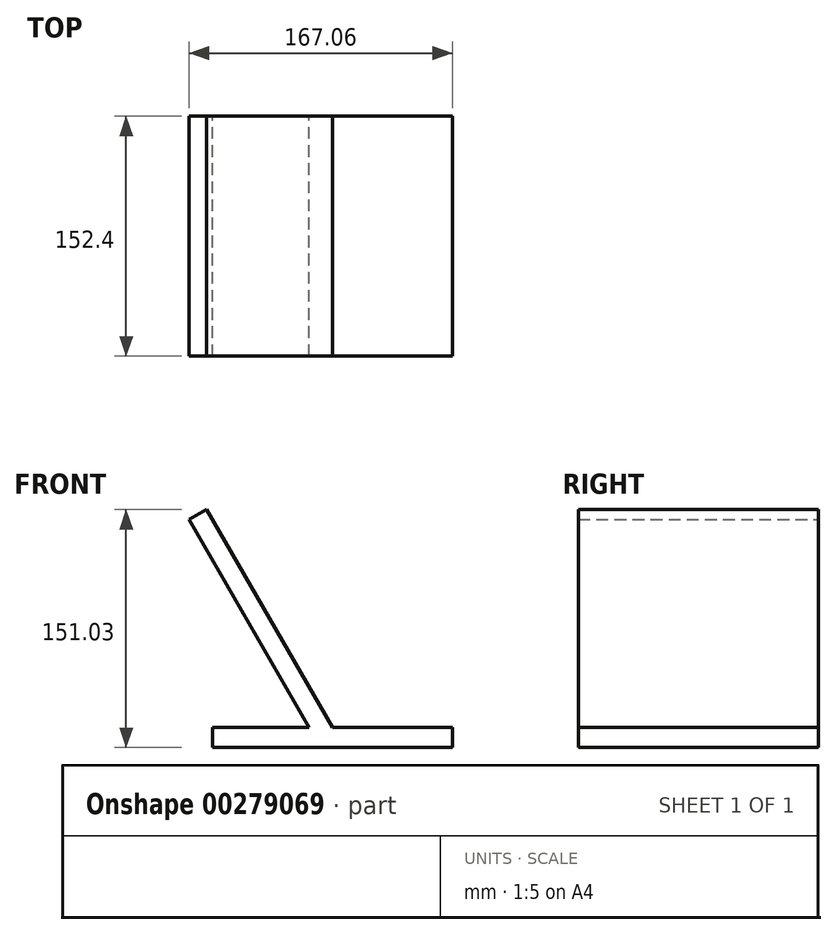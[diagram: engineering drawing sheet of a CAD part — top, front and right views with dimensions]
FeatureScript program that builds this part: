
annotation { "Feature Type Name" : "Feature", "Feature Type Description" : "" }
export const myFeature = defineFeature(function(context is Context, id is Id, definition is map)
    precondition{}
    {
        {
            var Q0;
            Q0=qCreatedBy(makeId("Top.planeOp"),FACE);
            var sketch = newSketch(context, id + "F0", { "sketchPlane" : qUnion([Q0])});
            skLineSegment(sketch, "E0.bottom", {"start": v(76.2, -76.2) * mm, "end": v(-76.2, -76.2) * mm});
            skLineSegment(sketch, "E0.top", {"start": v(76.2, 76.2) * mm, "end": v(-76.2, 76.2) * mm});
            skLineSegment(sketch, "E0.left", {"start": v(76.2, -76.2) * mm, "end": v(76.2, 76.2) * mm});
            skLineSegment(sketch, "E0.right", {"start": v(-76.2, -76.2) * mm, "end": v(-76.2, 76.2) * mm});
            skPoint(sketch, "E0.middle", {"position": v(0, 0) * mm});
            skSolve(sketch);
        }
        {
            var Q0;
            Q0 = qSketchRegion(id + "F0", true);
            extrude(context, id + "F1", {"entities" : qUnion([Q0]), "oppositeDirection" : true, "depth" : 12.7 * mm});
        }
        {
            var Q0;
            Q0=qCreatedBy(makeId("Front.planeOp"),FACE);
            var sketch = newSketch(context, id + "F2", { "sketchPlane" : qUnion([Q0])});
            skLineSegment(sketch, "E1", {"start": v(0, 0) * mm, "end": v(-79.87, 138.33) * mm});
            skLineSegment(sketch, "E2", {"start": v(-79.87, 138.33) * mm, "end": v(-90.86, 131.98) * mm});
            skLineSegment(sketch, "E3", {"start": v(-90.86, 131.98) * mm, "end": v(-14.66, 0) * mm});
            skLineSegment(sketch, "E4", {"start": v(-14.66, 0) * mm, "end": v(0, 0) * mm});
            skSolve(sketch);
        }
        {
            var Q0;
            Q0=makeQuery(id+"F2.imprint","IMPRINT",FACE,{"disambiguationData":[TD([[makeQuery(id+"F2.imprint","IMPRINT",EDGE,{"derivedFrom":sQuery(id+"F2.wireOp",EDGE,"E1")}),1.0]])]});
            extrude(context, id + "F3", {"entities" : qUnion([Q0]), "operationType" : NewBodyOperationType.ADD, "endBound" : BoundingType.SYMMETRIC, "depth" : 152.4 * mm});
        }
    });
